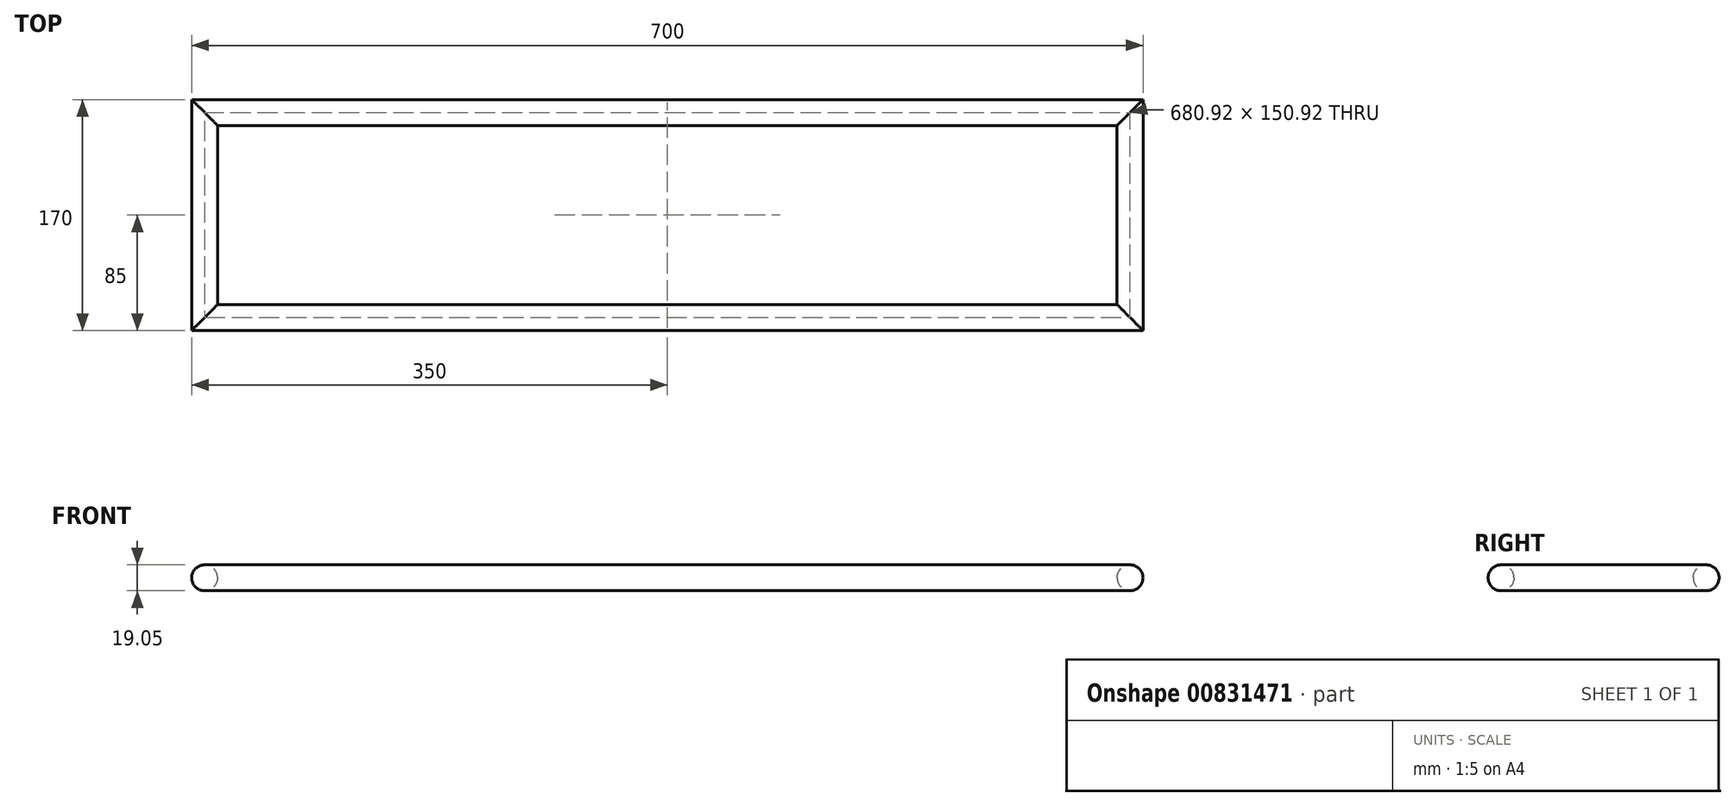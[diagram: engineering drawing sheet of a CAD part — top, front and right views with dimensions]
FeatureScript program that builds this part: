
annotation { "Feature Type Name" : "Feature", "Feature Type Description" : "" }
export const myFeature = defineFeature(function(context is Context, id is Id, definition is map)
    precondition{}
    {
        {
            var Q0;
            Q0=qCreatedBy(makeId("Top.planeOp"),FACE);
            var sketch = newSketch(context, id + "F0", { "sketchPlane" : qUnion([Q0])});
            skLineSegment(sketch, "E0.bottom", {"start": v(350, 85) * mm, "end": v(-350, 85) * mm});
            skLineSegment(sketch, "E0.top", {"start": v(350, -85) * mm, "end": v(-350, -85) * mm});
            skLineSegment(sketch, "E0.left", {"start": v(350, 85) * mm, "end": v(350, -85) * mm});
            skLineSegment(sketch, "E0.right", {"start": v(-350, 85) * mm, "end": v(-350, -85) * mm});
            skPoint(sketch, "E0.middle", {"position": v(0, 0) * mm});
            skLineSegment(sketch, "E1.bottom", {"start": v(330.95, 65.95) * mm, "end": v(-330.95, 65.95) * mm});
            skLineSegment(sketch, "E1.top", {"start": v(330.95, -65.95) * mm, "end": v(-330.95, -65.95) * mm});
            skLineSegment(sketch, "E1.left", {"start": v(330.95, 65.95) * mm, "end": v(330.95, -65.95) * mm});
            skLineSegment(sketch, "E1.right", {"start": v(-330.95, 65.95) * mm, "end": v(-330.95, -65.95) * mm});
            skSolve(sketch);
        }
        {
            var Q0;
            Q0=makeQuery(id+"F0.imprint","IMPRINT",FACE,{"disambiguationData":[TD([[makeQuery(id+"F0.imprint","IMPRINT",EDGE,{"derivedFrom":sQuery(id+"F0.wireOp",EDGE,"E0.bottom")}),1.0]])]});
            extrude(context, id + "F1", {"entities" : qUnion([Q0]), "depth" : 19.05 * mm, "offsetDistance" : 25 * mm});
        }
        {
            var Q0;
            Q0=makeQuery(id+"F1.opExtrude","CAP_EDGE",EDGE,{"disambiguationData":[OSD([sQuery(id+"F0.wireOp",EDGE,"E0.top")])],"isStart":true});
            var Q1;
            Q1=makeQuery(id+"F1.opExtrude","CAP_EDGE",EDGE,{"disambiguationData":[OSD([sQuery(id+"F0.wireOp",EDGE,"E0.left")])],"isStart":true});
            var Q2;
            Q2=makeQuery(id+"F1.opExtrude","CAP_EDGE",EDGE,{"disambiguationData":[OSD([sQuery(id+"F0.wireOp",EDGE,"E0.bottom")])],"isStart":true});
            var Q3;
            Q3=makeQuery(id+"F1.opExtrude","CAP_EDGE",EDGE,{"disambiguationData":[OSD([sQuery(id+"F0.wireOp",EDGE,"E0.right")])],"isStart":true});
            var Q4;
            Q4=makeQuery(id+"F1.opExtrude","CAP_EDGE",EDGE,{"disambiguationData":[OSD([sQuery(id+"F0.wireOp",EDGE,"E1.right")])],"isStart":true});
            var Q5;
            Q5=makeQuery(id+"F1.opExtrude","CAP_EDGE",EDGE,{"disambiguationData":[OSD([sQuery(id+"F0.wireOp",EDGE,"E1.bottom")])],"isStart":true});
            var Q6;
            Q6=makeQuery(id+"F1.opExtrude","CAP_EDGE",EDGE,{"disambiguationData":[OSD([sQuery(id+"F0.wireOp",EDGE,"E1.top")])],"isStart":true});
            var Q7;
            Q7=makeQuery(id+"F1.opExtrude","CAP_EDGE",EDGE,{"disambiguationData":[OSD([sQuery(id+"F0.wireOp",EDGE,"E1.left")])],"isStart":true});
            var Q8;
            Q8=makeQuery(id+"F1.opExtrude","CAP_EDGE",EDGE,{"disambiguationData":[OSD([sQuery(id+"F0.wireOp",EDGE,"E0.top")])],"isStart":false});
            var Q9;
            Q9=makeQuery(id+"F1.opExtrude","CAP_EDGE",EDGE,{"disambiguationData":[OSD([sQuery(id+"F0.wireOp",EDGE,"E0.left")])],"isStart":false});
            var Q10;
            Q10=makeQuery(id+"F1.opExtrude","CAP_EDGE",EDGE,{"disambiguationData":[OSD([sQuery(id+"F0.wireOp",EDGE,"E1.bottom")])],"isStart":false});
            var Q11;
            Q11=makeQuery(id+"F1.opExtrude","CAP_EDGE",EDGE,{"disambiguationData":[OSD([sQuery(id+"F0.wireOp",EDGE,"E1.right")])],"isStart":false});
            var Q12;
            Q12=makeQuery(id+"F1.opExtrude","CAP_EDGE",EDGE,{"disambiguationData":[OSD([sQuery(id+"F0.wireOp",EDGE,"E0.right")])],"isStart":false});
            var Q13;
            Q13=makeQuery(id+"F1.opExtrude","CAP_EDGE",EDGE,{"disambiguationData":[OSD([sQuery(id+"F0.wireOp",EDGE,"E0.bottom")])],"isStart":false});
            var Q14;
            Q14=makeQuery(id+"F1.opExtrude","CAP_EDGE",EDGE,{"disambiguationData":[OSD([sQuery(id+"F0.wireOp",EDGE,"E1.top")])],"isStart":false});
            var Q15;
            Q15=makeQuery(id+"F1.opExtrude","CAP_EDGE",EDGE,{"disambiguationData":[OSD([sQuery(id+"F0.wireOp",EDGE,"E1.left")])],"isStart":false});
            fillet(context, id + "F2", {"entities" : qUnion([Q0, Q1, Q2, Q3, Q4, Q5, Q6, Q7, Q8, Q9, Q10, Q11, Q12, Q13, Q14, Q15]), "radius" : 9.5 * mm, "tangentPropagation" : true, "allowEdgeOverflow" : false});
        }
    });
